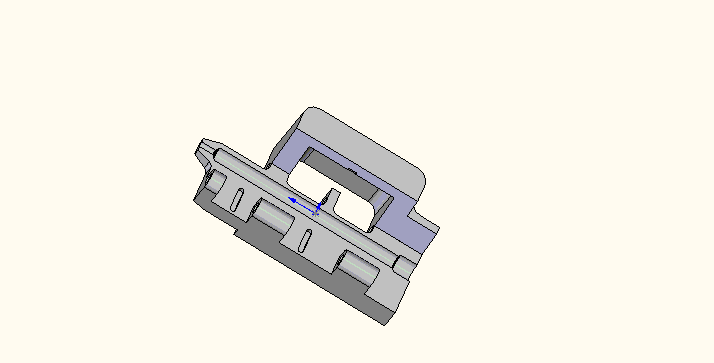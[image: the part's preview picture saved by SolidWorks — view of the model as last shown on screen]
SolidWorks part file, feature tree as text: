
SOLIDWORKS PART (.sldprt)
format: sldprt  version: not decoded by parser v0  size: 1,706,496 bytes
history: native  units: mm
features: sketch x24, cut_extrude x16, extrude x5, fillet x5, cut_revolve x2, material x1, chamfer x1 (+13 scaffold rows collapsed; 3 parser-record rows omitted)
feature tree (70):
  scaffold x13  (default folders/planes/origin — collapsed)
  material  "6061 Alloy"
  sketch  "BottomS"  dims[c1.Holder_W=13.97mm c1.Fiber_H=0.0mm c1.D3=6.35mm c1.D4=7.62mm c1.Holder_E=0.0mm c2.Holder_W=0.0mm c2.Holder_E=0.0mm]
  parser-record x3  (decoder bookkeeping rows leaked as tree rows — omitted from the tree; the rows remain in map.json)
  extrude  "Bottom"  Depth=0mm
  sketch  "HingeBlockS"  dims[c1.D2=1.5875mm c1.D1=3.175mm c2.D2=3.175mm c2.D1=3.175mm c3.D2=3.175mm c3.D1=3.175mm c3.Axle_Block_H=3.81mm c3.Hinge_Block_H=0.0mm]
  extrude  "Hinge Block"  [1 undecoded]
  sketch  "KevlarHoleS"  dims[c1.D1=1.1938mm c1.Fiber_Kevlar_R=0.0mm c1.Fiber_Kevlar_D=0.0mm c2.D1=~3.340655mm]
  cut_extrude  "Kevlar Hole"  [1 undecoded]
  sketch  "HeatShrinkS"  dims[D1=4.445mm]
  cut_extrude  "Heat Shrink"  Depth=2.54mm
  sketch  "Sketch71"  dims[c1.D1=~2.414368mm c2.D1=59.0deg]
  cut_revolve  "Entry Chamfer"  Angle=360deg
  sketch  "LatchAxleS"  dims[D1=1.5875mm D2=0.0mm D3=0.0mm]
  cut_extrude  "Latch Axle"  [1 undecoded]
  sketch  "WingS"  dims[c1.D1=3.175mm c1.D2=12.065mm c2.D2=75.0deg c2.D3=~10.913877mm c3.D3=5.0deg c3.D4=1.778mm c3.D5=12.7mm c4.D4=~2.38887mm c5.D4=~41.902273deg c6.D4=2.032mm c6.Wing_Top_W=0.0mm c6.Wing_H=0.0mm c6.D3=0.0mm c6.D7=~4.785597mm c7.D7=10.0deg c7.D4=5.715mm c8.D7=~5.155585mm c9.D7=60.0deg c9.D2=4.826mm c10.D2=90.0deg c10.Wing_W=0.0mm c10.D3=~6.48281mm c11.D3=0.0deg c12.D3=1.27mm c12.D4=~5.31832mm c12.Wing_Int_A=0.0deg c12.D7=~4.326464mm c13.D7=80.0deg c13.D8=5.715mm c14.D7=~7.360355mm c14.Wing_Ext_A=0.0deg c14.Wing_E=0.0mm c14.D1=1.27mm]
  sketch  "GuideClearanceS"  dims[D3=~0.79375mm Guide_Clearance_L=0.0mm Guide_Clearance_E=0.0mm]
  cut_extrude  "Guide Clearance"  [1 undecoded]
  sketch  "FrontClearanceS"  dims[D1=0.0mm D2=7.112mm]
  cut_extrude  "Front Clearance"  [1 undecoded]
  sketch  "NoseChannelS"  dims[D1=0.0mm]
  extrude  "Nose Channel"  [1 undecoded]
  sketch  "NoseCut1S"  dims[D1=0.0mm]
  cut_extrude  "Nose Cut 1"  Depth=3.175mm
  sketch  "Sketch59"  dims[c1.D1=1.1811mm c2.D1=59.0deg]
  cut_revolve  "Buffer Chamfer"  Angle=360deg
  fillet  "Fillet2"  Radius=0.79375mm
  sketch  "Sketch63"  dims[c1.D1=1.27mm c1.D2=~4.747856mm c2.D2=70.0deg c2.D1=3.556mm c2.D3=6.096mm c2.D4=5.715mm]
  extrude  "Wing"  [1 undecoded]
  sketch  "LatchClearanceS"  dims[c1.D3=~0.79375mm c1.D1=0.0mm c1.D2=0.0mm c2.D3=0.0mm c2.D4=2.032mm c2.D5=1.27mm c3.D3=1.27mm c3.D6=1.5875mm]
  cut_extrude  "Latch Clearance"  Depth=1.27mm
  fillet  "Fillet3"  Radius=1.5875mm
  sketch  "Sketch65"  dims[c1.D1=1.016mm c1.D2=0.762mm c1.D3=2.032mm c1.D4=2.032mm c2.D3=2.032mm]
  cut_extrude  "Latch Spring Holes"  Depth=2.54mm
  sketch  "Sketch67"  dims[c1.D1=1.27mm c1.D2=3.556mm c1.D3=5.08mm c1.D4=2.54mm c1.D5=2.54mm c1.D6=4.445mm c1.D7=3.175mm c2.D7=0.086deg c3.D7=2.667mm c3.D8=2.794mm c3.D9=2.5908mm c3.D10=1.905mm c3.D4=0.0508mm c3.D5=0.0508mm c4.D4=2.286mm c4.D5=2.54mm c4.D9=2.54mm c4.D7=2.54mm c4.D8=2.54mm c5.D9=3.048mm c5.D4=2.286mm c5.D7=3.175mm]
  cut_extrude  "Hinge Clearance"  [1 undecoded]
  sketch  "NoseCut2S"  dims[c1.D1=0.0mm c1.D2=~6.423375mm c2.D2=75.0deg]
  cut_extrude  "Nose Cut 2"  [1 undecoded]
  sketch  "Sketch69"  dims[D1=0.762mm D2=0.762mm]
  cut_extrude  "Flat Clearance"  Depth=0.254mm
  sketch  "Sketch62"  dims[c1.D1=~2.38125mm c1.D3=~2.38125mm c1.D2=3.175mm c2.D3=3.175mm c2.D4=15.24mm]
  cut_extrude  "Alignment Holes"  Depth=2.54mm
  sketch  "Sketch61"  dims[D4=0.508mm D1=3.6068mm D2=10.16mm D3=1.27mm]
  cut_extrude  "Magnet"  Depth=2.35mm
  chamfer  "Chamfer1"  Distance=0.254mm Angle=45deg
  sketch  "Sketch70"  dims[c1.D4=~0.396875mm c1.D1=~0.79375mm c1.D2=4.191mm c1.D3=2.667mm c2.D1=~0.79375mm c2.D4=0.762mm c2.D5=2.667mm]
  cut_extrude  "Spring Retaining Slots"  Depth=0.508mm
  sketch  "Sketch72"  dims[D1=1.5621mm]
  extrude  "Latch Shaft Interference Fit"  Depth=6.35mm
  sketch  "Sketch74"
  cut_extrude  "Cut-Extrude1"  [1 undecoded]
  sketch  "Sketch76"  dims[D1=3.556mm D2=1.27mm]
  cut_extrude  "Cut-Extrude2"  Depth=2.794mm
  fillet  "Fillet4"  Radius=1.5875mm
  fillet  "Fillet5"  Radius=0.79375mm
  fillet  "Fillet6"  Radius=1.905mm Fiber_H=3.429mm Holder_W=0mm Axle_Block_H=3.81mm Fiber_Kevlar_D=2.3622mm Fiber_Buffer)D=0.708683mm Fiber_Buffer_D=0.708683mm Heat_Shrink_D=4.826mm Wing_H=12.7mm Wing_Top_W=1.524mm Wing_Ext_A=75deg Wing_W=3.81mm Wing_E=5.715mm Guide_Clearance_E=2.032mm Guide_Clearance_L=7.112mm Clamping_Flat_E=0mm
decode coverage: 42 of 53 modeling features carry decoded parameters
note: ~ marks probable driven/reference dimensions
note: 10 parameter values undecoded
summary: no parameter record found for 10 features
note: suppression state not decoded; provenance and decode notes live in map.json
